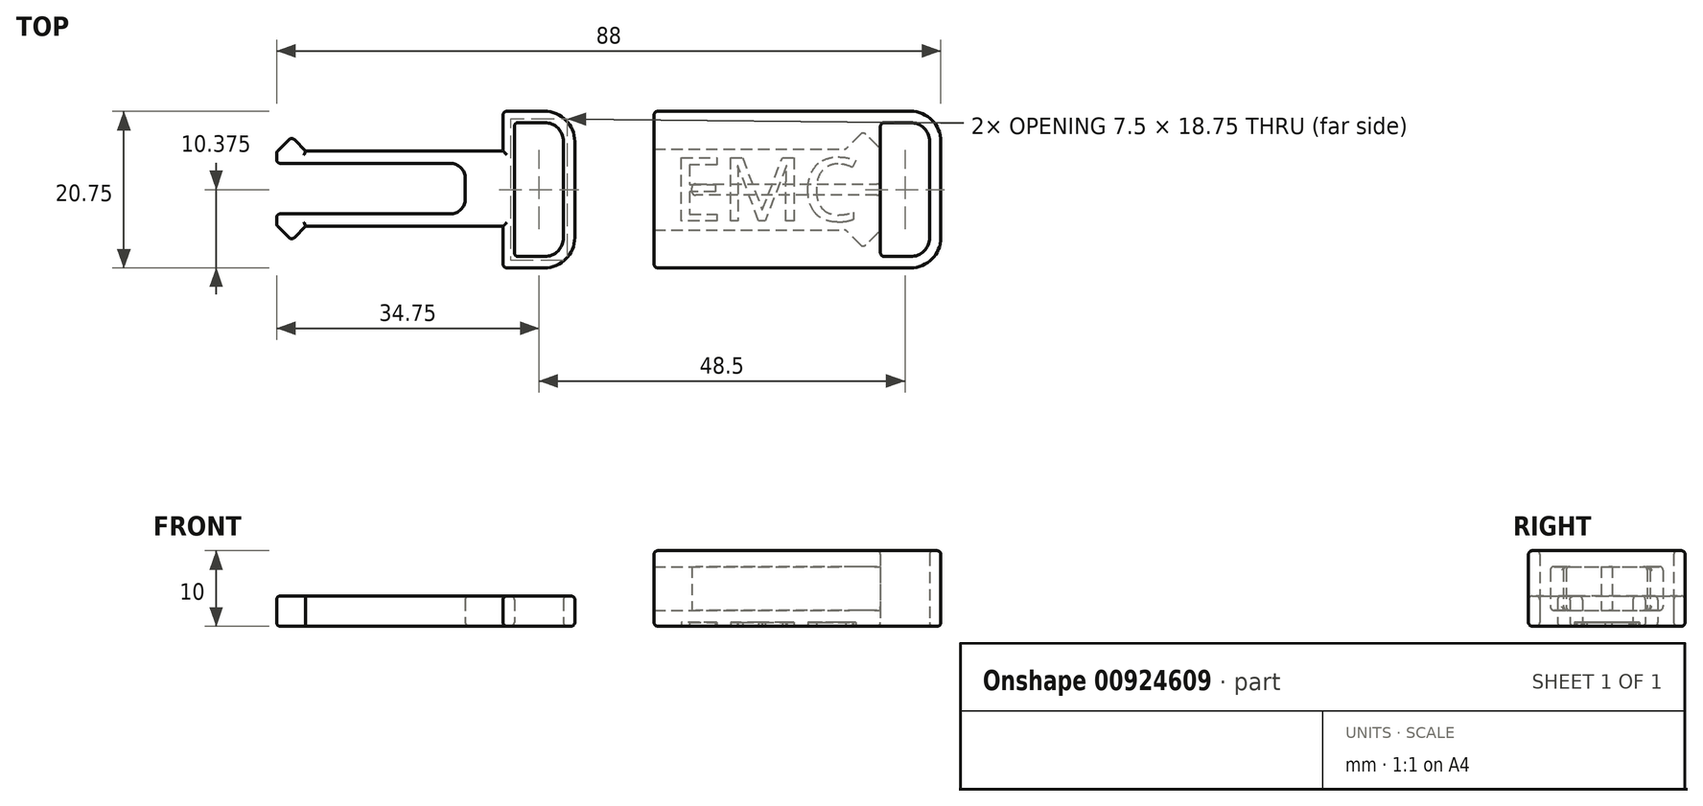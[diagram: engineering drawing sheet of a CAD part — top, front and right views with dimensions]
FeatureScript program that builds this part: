
annotation { "Feature Type Name" : "Feature", "Feature Type Description" : "" }
export const myFeature = defineFeature(function(context is Context, id is Id, definition is map)
    precondition{}
    {
        {
            var Q0;
            Q0=qCreatedBy(makeId("Top.planeOp"),FACE);
            var sketch = newSketch(context, id + "F0", { "sketchPlane" : qUnion([Q0])});
            skLineSegment(sketch, "E0", {"start": v(-39.85, 10) * mm, "end": v(-38.35, 11.5) * mm});
            skLineSegment(sketch, "E1", {"start": v(-37.65, 11.5) * mm, "end": v(-36.15, 10) * mm});
            skLineSegment(sketch, "E2", {"start": v(-36.15, 10) * mm, "end": v(-10, 10) * mm});
            skLineSegment(sketch, "E3", {"start": v(-10, 0) * mm, "end": v(-36.15, 0) * mm});
            skLineSegment(sketch, "E4", {"start": v(-36.15, 0) * mm, "end": v(-37.65, -1.5) * mm});
            skLineSegment(sketch, "E5", {"start": v(-38.35, -1.5) * mm, "end": v(-39.85, 0) * mm});
            skLineSegment(sketch, "E6", {"start": v(-40, 0.35) * mm, "end": v(-40, 1.15) * mm});
            skLineSegment(sketch, "E7", {"start": v(-39.5, 1.65) * mm, "end": v(-17, 1.65) * mm});
            skLineSegment(sketch, "E8", {"start": v(-15, 3.65) * mm, "end": v(-15, 6.35) * mm});
            skLineSegment(sketch, "E9", {"start": v(-17, 8.35) * mm, "end": v(-39.5, 8.35) * mm});
            skLineSegment(sketch, "E10", {"start": v(-40, 8.85) * mm, "end": v(-40, 9.65) * mm});
            skPoint(sketch, "E11.visualSharp", {"position": v(-15, 8.35) * mm});
            skArc(sketch, "E11.filletArc", {"start": v(-15, 6.35) * mm, "mid": v(-15.59, 7.77) * mm, "end": v(-17, 8.35) * mm});
            skPoint(sketch, "E12.visualSharp", {"position": v(-15, 1.65) * mm});
            skArc(sketch, "E12.filletArc", {"start": v(-17, 1.65) * mm, "mid": v(-15.59, 2.23) * mm, "end": v(-15, 3.65) * mm});
            skPoint(sketch, "E13.visualSharp", {"position": v(-38, 11.85) * mm});
            skArc(sketch, "E13.filletArc", {"start": v(-37.65, 11.5) * mm, "mid": v(-38, 11.65) * mm, "end": v(-38.35, 11.5) * mm});
            skPoint(sketch, "E14.visualSharp", {"position": v(-38, -1.85) * mm});
            skArc(sketch, "E14.filletArc", {"start": v(-38.35, -1.5) * mm, "mid": v(-38, -1.65) * mm, "end": v(-37.65, -1.5) * mm});
            skPoint(sketch, "E15.visualSharp", {"position": v(-40, 0.15) * mm});
            skArc(sketch, "E15.filletArc", {"start": v(-40, 0.35) * mm, "mid": v(-39.96, 0.16) * mm, "end": v(-39.85, 0) * mm});
            skPoint(sketch, "E16.visualSharp", {"position": v(-40, 1.65) * mm});
            skArc(sketch, "E16.filletArc", {"start": v(-39.5, 1.65) * mm, "mid": v(-39.85, 1.5) * mm, "end": v(-40, 1.15) * mm});
            skPoint(sketch, "E17.visualSharp", {"position": v(-40, 8.35) * mm});
            skArc(sketch, "E17.filletArc", {"start": v(-40, 8.85) * mm, "mid": v(-39.85, 8.5) * mm, "end": v(-39.5, 8.35) * mm});
            skPoint(sketch, "E18.visualSharp", {"position": v(-40, 9.85) * mm});
            skArc(sketch, "E18.filletArc", {"start": v(-39.85, 10) * mm, "mid": v(-39.96, 9.84) * mm, "end": v(-40, 9.65) * mm});
            skLineSegment(sketch, "E19.bottom", {"start": v(10, -0.5) * mm, "end": v(35.2, -0.5) * mm});
            skLineSegment(sketch, "E19.top", {"start": v(10, 10.25) * mm, "end": v(35.2, 10.25) * mm});
            skLineSegment(sketch, "E19.left", {"start": v(10, -0.5) * mm, "end": v(10, 10.25) * mm});
            skLineSegment(sketch, "E20", {"start": v(10, 4.88) * mm, "end": v(40, 4.88) * mm, "construction": true});
            skLineSegment(sketch, "E21", {"start": v(39.5, 4.13) * mm, "end": v(15.5, 4.13) * mm});
            skLineSegment(sketch, "E22", {"start": v(15, 4.63) * mm, "end": v(15, 5.13) * mm});
            skLineSegment(sketch, "E23", {"start": v(15.5, 5.63) * mm, "end": v(39.5, 5.63) * mm});
            skLineSegment(sketch, "E24", {"start": v(39.57, 10.68) * mm, "end": v(38.05, 12.2) * mm});
            skLineSegment(sketch, "E25", {"start": v(37.35, 12.2) * mm, "end": v(35.55, 10.4) * mm});
            skLineSegment(sketch, "E26", {"start": v(39.57, -0.93) * mm, "end": v(38.05, -2.45) * mm});
            skLineSegment(sketch, "E27", {"start": v(37.35, -2.45) * mm, "end": v(35.55, -0.65) * mm});
            skLineSegment(sketch, "E28", {"start": v(-10, 0) * mm, "end": v(10, 0) * mm, "construction": true});
            skLineSegment(sketch, "E29", {"start": v(-10, 10) * mm, "end": v(10, 10) * mm, "construction": true});
            skPoint(sketch, "E30.visualSharp", {"position": v(37.7, 12.55) * mm});
            skArc(sketch, "E30.filletArc", {"start": v(38.05, 12.2) * mm, "mid": v(37.7, 12.34) * mm, "end": v(37.35, 12.2) * mm});
            skPoint(sketch, "E31.visualSharp", {"position": v(37.7, -2.8) * mm});
            skArc(sketch, "E31.filletArc", {"start": v(37.35, -2.45) * mm, "mid": v(37.7, -2.6) * mm, "end": v(38.05, -2.45) * mm});
            skPoint(sketch, "E32.visualSharp", {"position": v(35.4, -0.5) * mm});
            skArc(sketch, "E32.filletArc", {"start": v(35.55, -0.65) * mm, "mid": v(35.38, -0.54) * mm, "end": v(35.2, -0.5) * mm});
            skPoint(sketch, "E33.visualSharp", {"position": v(35.4, 10.25) * mm});
            skArc(sketch, "E33.filletArc", {"start": v(35.2, 10.25) * mm, "mid": v(35.38, 10.29) * mm, "end": v(35.55, 10.4) * mm});
            skPoint(sketch, "E34.visualSharp", {"position": v(15, 4.13) * mm});
            skArc(sketch, "E34.filletArc", {"start": v(15, 4.63) * mm, "mid": v(15.15, 4.27) * mm, "end": v(15.5, 4.13) * mm});
            skPoint(sketch, "E35.visualSharp", {"position": v(15, 5.63) * mm});
            skArc(sketch, "E35.filletArc", {"start": v(15.5, 5.63) * mm, "mid": v(15.15, 5.48) * mm, "end": v(15, 5.13) * mm});
            skLineSegment(sketch, "E36", {"start": v(10, 10.25) * mm, "end": v(10, 15.25) * mm});
            skLineSegment(sketch, "E37", {"start": v(10, 15.25) * mm, "end": v(40, 15.25) * mm});
            skLineSegment(sketch, "E38", {"start": v(40, 10.85) * mm, "end": v(40, 15.25) * mm});
            skLineSegment(sketch, "E39", {"start": v(10, -0.5) * mm, "end": v(10, -5.5) * mm});
            skLineSegment(sketch, "E40", {"start": v(10, -5.5) * mm, "end": v(40, -5.5) * mm});
            skLineSegment(sketch, "E41", {"start": v(40, -5.5) * mm, "end": v(40, -1.1) * mm});
            skLineSegment(sketch, "E42", {"start": v(40, 4.63) * mm, "end": v(40, 5.13) * mm});
            skPoint(sketch, "E43.visualSharp", {"position": v(40, 5.63) * mm});
            skArc(sketch, "E43.filletArc", {"start": v(40, 5.13) * mm, "mid": v(39.85, 5.48) * mm, "end": v(39.5, 5.63) * mm});
            skPoint(sketch, "E44.visualSharp", {"position": v(40, 4.13) * mm});
            skArc(sketch, "E44.filletArc", {"start": v(39.5, 4.13) * mm, "mid": v(39.85, 4.27) * mm, "end": v(40, 4.63) * mm});
            skPoint(sketch, "E45.visualSharp", {"position": v(40, 10.25) * mm});
            skArc(sketch, "E45.filletArc", {"start": v(39.57, 10.68) * mm, "mid": v(39.85, 10.62) * mm, "end": v(40, 10.85) * mm});
            skPoint(sketch, "E46.visualSharp", {"position": v(40, -0.5) * mm});
            skArc(sketch, "E46.filletArc", {"start": v(40, -1.1) * mm, "mid": v(39.85, -0.87) * mm, "end": v(39.57, -0.93) * mm});
            skLineSegment(sketch, "E47", {"start": v(40, 15.25) * mm, "end": v(44, 15.25) * mm});
            skLineSegment(sketch, "E48", {"start": v(48, 11.25) * mm, "end": v(48, -1.5) * mm});
            skLineSegment(sketch, "E49", {"start": v(44, -5.5) * mm, "end": v(40, -5.5) * mm});
            skPoint(sketch, "E50.visualSharp", {"position": v(48, 15.25) * mm});
            skArc(sketch, "E50.filletArc", {"start": v(48, 11.25) * mm, "mid": v(46.83, 14.08) * mm, "end": v(44, 15.25) * mm});
            skPoint(sketch, "E51.visualSharp", {"position": v(48, -5.5) * mm});
            skArc(sketch, "E51.filletArc", {"start": v(44, -5.5) * mm, "mid": v(46.83, -4.33) * mm, "end": v(48, -1.5) * mm});
            skLineSegment(sketch, "E52.0", {"start": v(44, -4) * mm, "end": v(40, -4) * mm});
            skLineSegment(sketch, "E52.1", {"start": v(40, 13.75) * mm, "end": v(44, 13.75) * mm});
            skArc(sketch, "E52.2", {"start": v(46.5, 11.25) * mm, "mid": v(45.77, 13.02) * mm, "end": v(44, 13.75) * mm});
            skLineSegment(sketch, "E52.3", {"start": v(46.5, 11.25) * mm, "end": v(46.5, -1.5) * mm});
            skArc(sketch, "E52.4", {"start": v(44, -4) * mm, "mid": v(45.77, -3.27) * mm, "end": v(46.5, -1.5) * mm});
            skLineSegment(sketch, "E53", {"start": v(40, -1.1) * mm, "end": v(40, 4.63) * mm});
            skLineSegment(sketch, "E54", {"start": v(40, 5.13) * mm, "end": v(40, 10.85) * mm});
            skLineSegment(sketch, "E55", {"start": v(-10, 10) * mm, "end": v(-10, 15.25) * mm});
            skLineSegment(sketch, "E56", {"start": v(-10, 15.25) * mm, "end": v(-4.5, 15.25) * mm});
            skLineSegment(sketch, "E57", {"start": v(-0.5, 11.25) * mm, "end": v(-0.5, -1.5) * mm});
            skLineSegment(sketch, "E58", {"start": v(-4.5, -5.5) * mm, "end": v(-10, -5.5) * mm});
            skLineSegment(sketch, "E59", {"start": v(-10, -5.5) * mm, "end": v(-10, 0) * mm});
            skPoint(sketch, "E60.visualSharp", {"position": v(-0.5, 15.25) * mm});
            skArc(sketch, "E60.filletArc", {"start": v(-0.5, 11.25) * mm, "mid": v(-1.67, 14.08) * mm, "end": v(-4.5, 15.25) * mm});
            skPoint(sketch, "E61.visualSharp", {"position": v(-0.5, -5.5) * mm});
            skArc(sketch, "E61.filletArc", {"start": v(-4.5, -5.5) * mm, "mid": v(-1.67, -4.33) * mm, "end": v(-0.5, -1.5) * mm});
            skLineSegment(sketch, "E62.0", {"start": v(-4.5, -4) * mm, "end": v(-8.5, -4) * mm});
            skLineSegment(sketch, "E62.1", {"start": v(-8.5, 13.75) * mm, "end": v(-4.5, 13.75) * mm});
            skArc(sketch, "E62.2", {"start": v(-2, 11.25) * mm, "mid": v(-2.73, 13.02) * mm, "end": v(-4.5, 13.75) * mm});
            skLineSegment(sketch, "E62.3", {"start": v(-2, 11.25) * mm, "end": v(-2, -1.5) * mm});
            skArc(sketch, "E62.4", {"start": v(-4.5, -4) * mm, "mid": v(-2.73, -3.27) * mm, "end": v(-2, -1.5) * mm});
            skLineSegment(sketch, "E63", {"start": v(-8.5, -4) * mm, "end": v(-8.5, 13.75) * mm});
            skSolve(sketch);
        }
        {
            var Q0;
            Q0=makeQuery(id+"F0.imprint","IMPRINT",FACE,{"disambiguationData":[TD([[makeQuery(id+"F0.imprint","IMPRINT",EDGE,{"derivedFrom":sQuery(id+"F0.wireOp",EDGE,"E0")}),-1.0]])]});
            extrude(context, id + "F1", {"entities" : qUnion([Q0]), "depth" : 4 * mm, "offsetDistance" : 25 * mm});
        }
        {
            var Q0;
            Q0=makeQuery(id+"F0.imprint","IMPRINT",FACE,{"disambiguationData":[TD([[makeQuery(id+"F0.imprint","IMPRINT",EDGE,{"derivedFrom":sQuery(id+"F0.wireOp",EDGE,"E19.top")}),1.0]])]});
            var Q1;
            Q1=makeQuery(id+"F0.imprint","IMPRINT",FACE,{"disambiguationData":[TD([[makeQuery(id+"F0.imprint","IMPRINT",EDGE,{"derivedFrom":sQuery(id+"F0.wireOp",EDGE,"E19.bottom")}),-1.0]])]});
            var Q2;
            {var subQ4=sQuery(id+"F0.wireOp",EDGE,"E47");Q2=makeQuery(id+"F0.imprint","IMPRINT",FACE,{"disambiguationData":[TD([[makeQuery(id+"F0.imprint","IMPRINT",EDGE,{"derivedFrom":subQ4}),-1.0]])]});}
            var Q3;
            Q3=makeQuery(id+"F0.imprint","IMPRINT",FACE,{"disambiguationData":[TD([[makeQuery(id+"F0.imprint","IMPRINT",EDGE,{"derivedFrom":sQuery(id+"F0.wireOp",EDGE,"E21")}),-1.0]])]});
            var Q4;
            Q4=makeQuery(id+"F0.imprint","IMPRINT",FACE,{"disambiguationData":[TD([[makeQuery(id+"F0.imprint","IMPRINT",EDGE,{"derivedFrom":sQuery(id+"F0.wireOp",EDGE,"E19.bottom")}),1.0]])]});
            extrude(context, id + "F2", {"entities" : qUnion([Q0, Q1, Q2, Q3, Q4]), "depth" : 10 * mm, "offsetDistance" : 25 * mm});
        }
        {
            var Q0;
            Q0=makeQuery(id+"F0.imprint","IMPRINT",FACE,{"disambiguationData":[TD([[makeQuery(id+"F0.imprint","IMPRINT",EDGE,{"derivedFrom":sQuery(id+"F0.wireOp",EDGE,"E19.bottom")}),1.0]])]});
            extrude(context, id + "F3", {"entities" : qUnion([Q0]), "operationType" : NewBodyOperationType.REMOVE, "depth" : (10 - 2.1) * mm, "offsetDistance" : 25 * mm, "hasSecondDirection" : true, "secondDirectionOppositeDirection" : false, "secondDirectionDepth" : 2.1 * mm});
        }
        {
            var Q0;
            Q0=makeQuery(id+"F2.opExtrude","CAP_EDGE",EDGE,{"disambiguationData":[OSD([sQuery(id+"F0.wireOp",EDGE,"E40"),sQuery(id+"F0.wireOp",EDGE,"E49")])],"isStart":false});
            var Q1;
            Q1=makeQuery(id+"F2.opExtrude","CAP_EDGE",EDGE,{"disambiguationData":[OSD([sQuery(id+"F0.wireOp",EDGE,"E40"),sQuery(id+"F0.wireOp",EDGE,"E49")])],"isStart":true});
            var Q2;
            Q2=makeQuery(id+"F2.opExtrude","CAP_EDGE",EDGE,{"disambiguationData":[OSD([sQuery(id+"F0.wireOp",EDGE,"E38"),sQuery(id+"F0.wireOp",EDGE,"E41"),sQuery(id+"F0.wireOp",EDGE,"E42"),sQuery(id+"F0.wireOp",EDGE,"E53"),sQuery(id+"F0.wireOp",EDGE,"E54")])],"isStart":true});
            var Q3;
            Q3=makeQuery(id+"F2.opExtrude","CAP_EDGE",EDGE,{"disambiguationData":[OSD([sQuery(id+"F0.wireOp",EDGE,"E52.3")])],"isStart":true});
            var Q4;
            Q4=makeQuery(id+"F2.opExtrude","CAP_EDGE",EDGE,{"disambiguationData":[OSD([sQuery(id+"F0.wireOp",EDGE,"E38"),sQuery(id+"F0.wireOp",EDGE,"E41"),sQuery(id+"F0.wireOp",EDGE,"E42"),sQuery(id+"F0.wireOp",EDGE,"E53"),sQuery(id+"F0.wireOp",EDGE,"E54")])],"isStart":false});
            var Q5;
            Q5=makeQuery(id+"F2.opExtrude","CAP_EDGE",EDGE,{"disambiguationData":[OSD([sQuery(id+"F0.wireOp",EDGE,"E52.1")])],"isStart":false});
            var Q6;
            Q6=makeQuery(id+"F2.opExtrude","SWEPT_EDGE",EDGE,{"disambiguationData":[OSD([sQuery(id+"F0.wireOp",EDGE,"E38"),sQuery(id+"F0.wireOp",EDGE,"E52.1")])]});
            var Q7;
            Q7=makeQuery(id+"F2.opExtrude","SWEPT_EDGE",EDGE,{"disambiguationData":[OSD([sQuery(id+"F0.wireOp",EDGE,"E41"),sQuery(id+"F0.wireOp",EDGE,"E52.0")])]});
            var Q8;
            Q8=makeQuery(id+"F1.opExtrude","CAP_EDGE",EDGE,{"disambiguationData":[OSD([sQuery(id+"F0.wireOp",EDGE,"E3"),sQuery(id+"F0.wireOp",EDGE,"I6Gnt4y1-43mR-zavZ-Z8b0-1lFV4vwPwSQO")])],"isStart":false});
            var Q9;
            Q9=makeQuery(id+"F1.opExtrude","CAP_EDGE",EDGE,{"disambiguationData":[OSD([sQuery(id+"F0.wireOp",EDGE,"E3"),sQuery(id+"F0.wireOp",EDGE,"I6Gnt4y1-43mR-zavZ-Z8b0-1lFV4vwPwSQO")])],"isStart":true});
            var Q10;
            Q10=makeQuery(id+"F1.opExtrude","CAP_EDGE",EDGE,{"disambiguationData":[OSD([sQuery(id+"F0.wireOp",EDGE,"2c0ac38c-4777-48dc-a336-a047d9a29385.filletArc")])],"isStart":true});
            var Q11;
            Q11=makeQuery(id+"F2.opExtrude","CAP_FACE",FACE,{"disambiguationData":[OSD([sQuery(id+"F0.wireOp",EDGE,"E19.left"),sQuery(id+"F0.wireOp",EDGE,"E36"),sQuery(id+"F0.wireOp",EDGE,"E37"),sQuery(id+"F0.wireOp",EDGE,"E38"),sQuery(id+"F0.wireOp",EDGE,"E39"),sQuery(id+"F0.wireOp",EDGE,"E40"),sQuery(id+"F0.wireOp",EDGE,"E41"),sQuery(id+"F0.wireOp",EDGE,"E42"),sQuery(id+"F0.wireOp",EDGE,"E47"),sQuery(id+"F0.wireOp",EDGE,"E48"),sQuery(id+"F0.wireOp",EDGE,"E49"),sQuery(id+"F0.wireOp",EDGE,"E50.filletArc"),sQuery(id+"F0.wireOp",EDGE,"E51.filletArc"),sQuery(id+"F0.wireOp",EDGE,"E52.0"),sQuery(id+"F0.wireOp",EDGE,"E52.1"),sQuery(id+"F0.wireOp",EDGE,"E52.2"),sQuery(id+"F0.wireOp",EDGE,"E52.3"),sQuery(id+"F0.wireOp",EDGE,"E52.4"),sQuery(id+"F0.wireOp",EDGE,"E53"),sQuery(id+"F0.wireOp",EDGE,"E54")])],"isStart":false});
            var Q12;
            Q12=makeQuery(id+"F2.opExtrude","SWEPT_EDGE",EDGE,{"disambiguationData":[OSD([sQuery(id+"F0.wireOp",EDGE,"E39"),sQuery(id+"F0.wireOp",EDGE,"E40")])]});
            var Q13;
            Q13=makeQuery(id+"F2.opExtrude","CAP_EDGE",EDGE,{"disambiguationData":[OSD([sQuery(id+"F0.wireOp",EDGE,"E19.left"),sQuery(id+"F0.wireOp",EDGE,"E36"),sQuery(id+"F0.wireOp",EDGE,"E39")])],"isStart":true});
            var Q14;
            Q14=makeQuery(id+"F2.opExtrude","SWEPT_EDGE",EDGE,{"disambiguationData":[OSD([sQuery(id+"F0.wireOp",EDGE,"E36"),sQuery(id+"F0.wireOp",EDGE,"E37")])]});
            var Q15;
            Q15=makeQuery(id+"F1.opExtrude","CAP_EDGE",EDGE,{"disambiguationData":[OSD([sQuery(id+"F0.wireOp",EDGE,"wThcPGqB-BI5p-er4L-HnO4-RvEGJrd96pcF")])],"isStart":false});
            var Q16;
            Q16=makeQuery(id+"F3.boolean.opBoolean","COPY",EDGE,{"derivedFrom":makeQuery(id+"F3.opExtrude","CAP_EDGE",EDGE,{"disambiguationData":[OSD([sQuery(id+"F0.wireOp",EDGE,"E19.bottom")])],"isStart":false})});
            var Q17;
            Q17=makeQuery(id+"F3.boolean.opBoolean","COPY",EDGE,{"derivedFrom":makeQuery(id+"F3.opExtrude","CAP_EDGE",EDGE,{"disambiguationData":[OSD([sQuery(id+"F0.wireOp",EDGE,"E19.bottom")])],"isStart":true})});
            var Q18;
            Q18=makeQuery(id+"F3.boolean.opBoolean","COPY",EDGE,{"derivedFrom":makeQuery(id+"F3.opExtrude","SWEPT_EDGE",EDGE,{"disambiguationData":[OSD([sQuery(id+"F0.wireOp",EDGE,"E19.bottom"),sQuery(id+"F0.wireOp",EDGE,"E19.left"),sQuery(id+"F0.wireOp",EDGE,"E39")])]})});
            var Q19;
            Q19=makeQuery(id+"F3.boolean.opBoolean","COPY",EDGE,{"derivedFrom":makeQuery(id+"F3.opExtrude","CAP_EDGE",EDGE,{"disambiguationData":[OSD([sQuery(id+"F0.wireOp",EDGE,"E19.top")])],"isStart":false})});
            var Q20;
            Q20=makeQuery(id+"F3.boolean.opBoolean","COPY",EDGE,{"derivedFrom":makeQuery(id+"F3.opExtrude","CAP_EDGE",EDGE,{"disambiguationData":[OSD([sQuery(id+"F0.wireOp",EDGE,"E19.top")])],"isStart":true})});
            var Q21;
            Q21=makeQuery(id+"F1.opExtrude","CAP_EDGE",EDGE,{"disambiguationData":[OSD([sQuery(id+"F0.wireOp",EDGE,"E12.filletArc")])],"isStart":true});
            var Q22;
            Q22=makeQuery(id+"F1.opExtrude","CAP_EDGE",EDGE,{"disambiguationData":[OSD([sQuery(id+"F0.wireOp",EDGE,"E7")])],"isStart":false});
            var Q23;
            Q23=makeQuery(id+"F1.opExtrude","CAP_EDGE",EDGE,{"disambiguationData":[OSD([sQuery(id+"F0.wireOp",EDGE,"E62.3")])],"isStart":false});
            var Q24;
            Q24=makeQuery(id+"F1.opExtrude","CAP_EDGE",EDGE,{"disambiguationData":[OSD([sQuery(id+"F0.wireOp",EDGE,"E62.2")])],"isStart":true});
            var Q25;
            Q25=makeQuery(id+"F1.opExtrude","CAP_EDGE",EDGE,{"disambiguationData":[OSD([sQuery(id+"F0.wireOp",EDGE,"E55")])],"isStart":false});
            var Q26;
            Q26=makeQuery(id+"F1.opExtrude","CAP_EDGE",EDGE,{"disambiguationData":[OSD([sQuery(id+"F0.wireOp",EDGE,"E59")])],"isStart":false});
            var Q27;
            Q27=makeQuery(id+"F1.opExtrude","CAP_EDGE",EDGE,{"disambiguationData":[OSD([sQuery(id+"F0.wireOp",EDGE,"E58")])],"isStart":false});
            var Q28;
            Q28=makeQuery(id+"F1.opExtrude","SWEPT_EDGE",EDGE,{"disambiguationData":[OSD([sQuery(id+"F0.wireOp",EDGE,"E58"),sQuery(id+"F0.wireOp",EDGE,"E59")])]});
            var Q29;
            Q29=makeQuery(id+"F1.opExtrude","SWEPT_EDGE",EDGE,{"disambiguationData":[OSD([sQuery(id+"F0.wireOp",EDGE,"E55"),sQuery(id+"F0.wireOp",EDGE,"E56")])]});
            var Q30;
            Q30=makeQuery(id+"F1.opExtrude","SWEPT_FACE",FACE,{"disambiguationData":[OSD([sQuery(id+"F0.wireOp",EDGE,"E63")])]});
            var Q31;
            Q31=makeQuery(id+"F1.opExtrude","CAP_EDGE",EDGE,{"disambiguationData":[OSD([sQuery(id+"F0.wireOp",EDGE,"E56")])],"isStart":true});
            var Q32;
            Q32=makeQuery(id+"F1.opExtrude","CAP_EDGE",EDGE,{"disambiguationData":[OSD([sQuery(id+"F0.wireOp",EDGE,"E55")])],"isStart":true});
            var Q33;
            Q33=makeQuery(id+"F1.opExtrude","CAP_EDGE",EDGE,{"disambiguationData":[OSD([sQuery(id+"F0.wireOp",EDGE,"E59")])],"isStart":true});
            var Q34;
            Q34=makeQuery(id+"F1.opExtrude","CAP_EDGE",EDGE,{"disambiguationData":[OSD([sQuery(id+"F0.wireOp",EDGE,"E2")])],"isStart":true});
            var Q35;
            Q35=makeQuery(id+"F1.opExtrude","CAP_EDGE",EDGE,{"disambiguationData":[OSD([sQuery(id+"F0.wireOp",EDGE,"E2")])],"isStart":false});
            var Q36;
            Q36=makeQuery(id+"F3.boolean.opBoolean","COPY",EDGE,{"derivedFrom":makeQuery(id+"F3.opExtrude","CAP_EDGE",EDGE,{"disambiguationData":[OSD([sQuery(id+"F0.wireOp",EDGE,"E54")])],"isStart":true})});
            var Q37;
            Q37=makeQuery(id+"F3.boolean.opBoolean","COPY",EDGE,{"derivedFrom":makeQuery(id+"F3.opExtrude","CAP_EDGE",EDGE,{"disambiguationData":[OSD([sQuery(id+"F0.wireOp",EDGE,"E54")])],"isStart":false})});
            var Q38;
            Q38=makeQuery(id+"F3.boolean.opBoolean","COPY",EDGE,{"derivedFrom":makeQuery(id+"F3.opExtrude","CAP_EDGE",EDGE,{"disambiguationData":[OSD([sQuery(id+"F0.wireOp",EDGE,"E53")])],"isStart":false})});
            var Q39;
            Q39=makeQuery(id+"F3.boolean.opBoolean","COPY",EDGE,{"derivedFrom":makeQuery(id+"F3.opExtrude","CAP_EDGE",EDGE,{"disambiguationData":[OSD([sQuery(id+"F0.wireOp",EDGE,"E53")])],"isStart":true})});
            fillet(context, id + "F4", {"entities" : qUnion([Q0, Q1, Q2, Q3, Q4, Q5, Q6, Q7, Q8, Q9, Q10, Q11, Q12, Q13, Q14, Q15, Q16, Q17, Q18, Q19, Q20, Q21, Q22, Q23, Q24, Q25, Q26, Q27, Q28, Q29, Q30, Q31, Q32, Q33, Q34, Q35, Q36, Q37, Q38, Q39]), "radius" : .5 * mm, "tangentPropagation" : true, "allowEdgeOverflow" : false});
        }
        {
            var Q0;
            Q0=qCreatedBy(makeId("Top.planeOp"),FACE);
            var sketch = newSketch(context, id + "F5", { "sketchPlane" : qUnion([Q0])});
            skText(sketch, "E64", { "text": "EMC", "fontName": "NotoSans-Regular.ttf"});
            skLineSegment(sketch, "E65.0", {"start": v(10, 4.88) * mm, "end": v(40, 4.88) * mm, "construction": true});
            skPoint(sketch, "E66", {"position": v(25, 4.88) * mm});
            const initialGuessF5  = {"E64": [0.0125, 0.0007, 1, 0, 0.00845]};
            skSetInitialGuess(sketch, initialGuessF5);
            skSolve(sketch);
        }
        {
            var Q0;
            Q0 = qSketchRegion(id + "F5", true);
            extrude(context, id + "F6", {"entities" : qUnion([Q0]), "operationType" : NewBodyOperationType.REMOVE, "depth" : .5 * mm, "offsetDistance" : 25 * mm});
        }
    });
